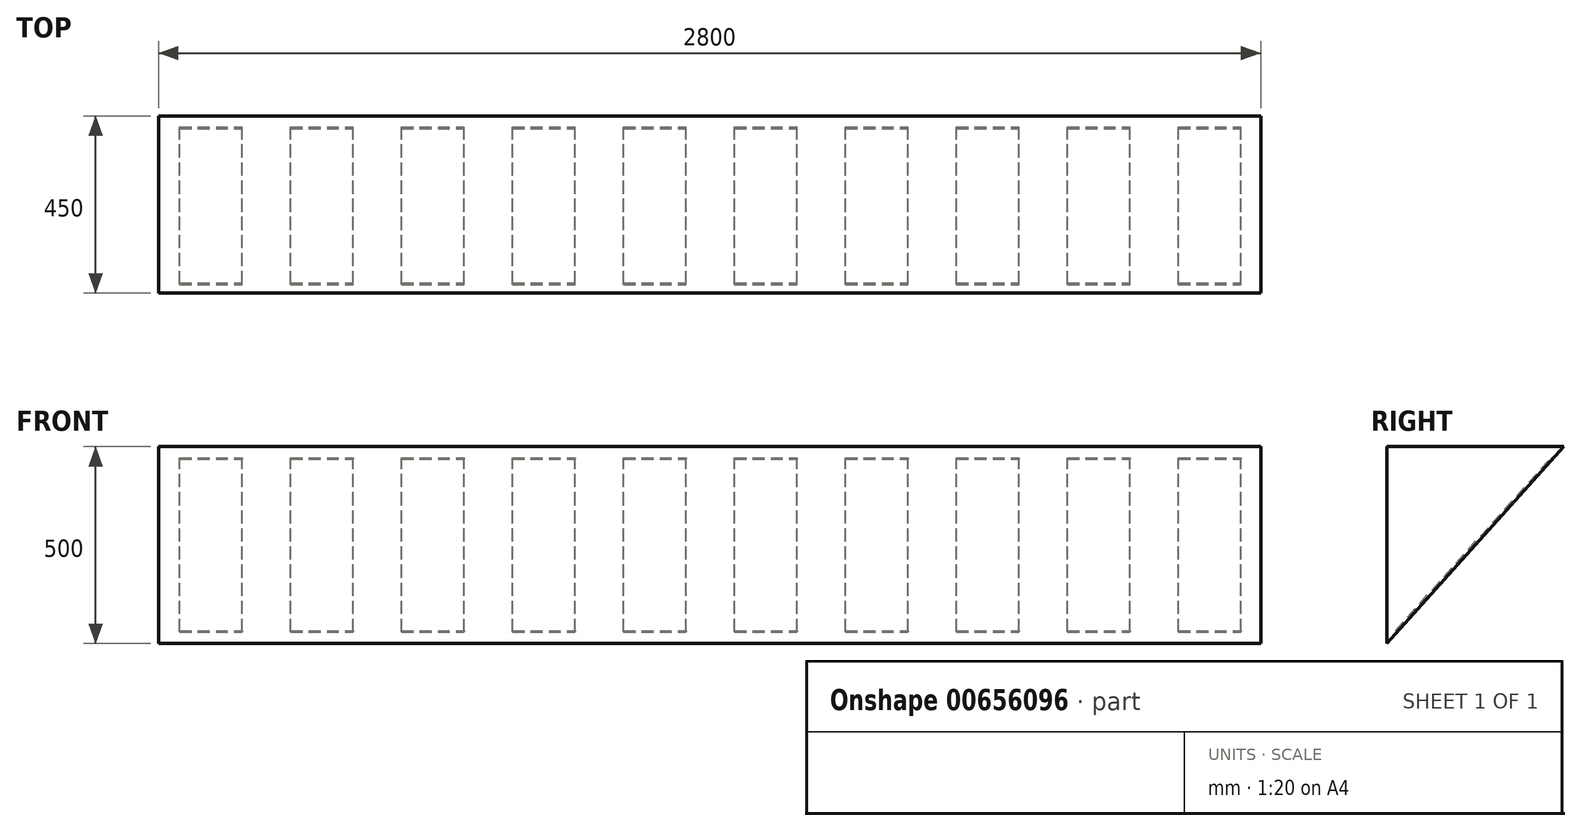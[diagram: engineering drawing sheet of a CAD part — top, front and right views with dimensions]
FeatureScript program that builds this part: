
annotation { "Feature Type Name" : "Feature", "Feature Type Description" : "" }
export const myFeature = defineFeature(function(context is Context, id is Id, definition is map)
    precondition{}
    {
        {
            var Q0;
            Q0=qCreatedBy(makeId("Right.planeOp"),FACE);
            var sketch = newSketch(context, id + "F0", { "sketchPlane" : qUnion([Q0])});
            skLineSegment(sketch, "E0", {"start": v(0, 0) * mm, "end": v(450, 0) * mm});
            skLineSegment(sketch, "E1", {"start": v(450, 0) * mm, "end": v(0, -500) * mm});
            skLineSegment(sketch, "E2", {"start": v(0, -500) * mm, "end": v(0, 0) * mm});
            skSolve(sketch);
        }
        {
            var Q0;
            Q0=makeQuery(id+"F0.imprint","IMPRINT",FACE,{"disambiguationData":[TD([[makeQuery(id+"F0.imprint","IMPRINT",EDGE,{"derivedFrom":sQuery(id+"F0.wireOp",EDGE,"E0")}),-1.0]])]});
            extrude(context, id + "F1", {"entities" : qUnion([Q0]), "depth" : 2800 * mm, "offsetDistance" : 25.4 * mm});
        }
        {
            var Q0;
            Q0=makeQuery(id+"F1.opExtrude","SWEPT_FACE",FACE,{"disambiguationData":[OSD([sQuery(id+"F0.wireOp",EDGE,"E1")])]});
            var sketch = newSketch(context, id + "F2", { "sketchPlane" : qUnion([Q0])});
            skLineSegment(sketch, "E3.bottom", {"start": v(-53.69, -332.56) * mm, "end": v(-212.32, -332.56) * mm});
            skLineSegment(sketch, "E3.top", {"start": v(-53.69, 258.3) * mm, "end": v(-212.32, 258.3) * mm});
            skLineSegment(sketch, "E3.left", {"start": v(-53.69, -332.56) * mm, "end": v(-53.69, 258.3) * mm});
            skLineSegment(sketch, "E3.right", {"start": v(-212.32, -332.56) * mm, "end": v(-212.32, 258.3) * mm});
            skLineSegment(sketch, "E4.1.0.0", {"start": v(-335.63, -332.56) * mm, "end": v(-494.26, -332.56) * mm});
            skLineSegment(sketch, "E4.1.0.1", {"start": v(-335.63, -332.56) * mm, "end": v(-335.63, 258.3) * mm});
            skLineSegment(sketch, "E4.1.0.2", {"start": v(-335.63, 258.3) * mm, "end": v(-494.26, 258.3) * mm});
            skLineSegment(sketch, "E4.1.0.3", {"start": v(-494.26, -332.56) * mm, "end": v(-494.26, 258.3) * mm});
            skLineSegment(sketch, "E4.2.0.0", {"start": v(-617.57, -332.56) * mm, "end": v(-776.2, -332.56) * mm});
            skLineSegment(sketch, "E4.2.0.1", {"start": v(-617.57, -332.56) * mm, "end": v(-617.57, 258.3) * mm});
            skLineSegment(sketch, "E4.2.0.2", {"start": v(-617.57, 258.3) * mm, "end": v(-776.2, 258.3) * mm});
            skLineSegment(sketch, "E4.2.0.3", {"start": v(-776.2, -332.56) * mm, "end": v(-776.2, 258.3) * mm});
            skLineSegment(sketch, "E4.3.0.0", {"start": v(-899.5, -332.56) * mm, "end": v(-1058.14, -332.56) * mm});
            skLineSegment(sketch, "E4.3.0.1", {"start": v(-899.5, -332.56) * mm, "end": v(-899.5, 258.3) * mm});
            skLineSegment(sketch, "E4.3.0.2", {"start": v(-899.5, 258.3) * mm, "end": v(-1058.14, 258.3) * mm});
            skLineSegment(sketch, "E4.3.0.3", {"start": v(-1058.14, -332.56) * mm, "end": v(-1058.14, 258.3) * mm});
            skLineSegment(sketch, "E4.4.0.0", {"start": v(-1181.45, -332.56) * mm, "end": v(-1340.08, -332.56) * mm});
            skLineSegment(sketch, "E4.4.0.1", {"start": v(-1181.45, -332.56) * mm, "end": v(-1181.45, 258.3) * mm});
            skLineSegment(sketch, "E4.4.0.2", {"start": v(-1181.45, 258.3) * mm, "end": v(-1340.08, 258.3) * mm});
            skLineSegment(sketch, "E4.4.0.3", {"start": v(-1340.08, -332.56) * mm, "end": v(-1340.08, 258.3) * mm});
            skLineSegment(sketch, "E4.5.0.0", {"start": v(-1463.39, -332.56) * mm, "end": v(-1622.02, -332.56) * mm});
            skLineSegment(sketch, "E4.5.0.1", {"start": v(-1463.39, -332.56) * mm, "end": v(-1463.39, 258.3) * mm});
            skLineSegment(sketch, "E4.5.0.2", {"start": v(-1463.39, 258.3) * mm, "end": v(-1622.02, 258.3) * mm});
            skLineSegment(sketch, "E4.5.0.3", {"start": v(-1622.02, -332.56) * mm, "end": v(-1622.02, 258.3) * mm});
            skLineSegment(sketch, "E4.6.0.0", {"start": v(-1745.33, -332.56) * mm, "end": v(-1903.96, -332.56) * mm});
            skLineSegment(sketch, "E4.6.0.1", {"start": v(-1745.33, -332.56) * mm, "end": v(-1745.33, 258.3) * mm});
            skLineSegment(sketch, "E4.6.0.2", {"start": v(-1745.33, 258.3) * mm, "end": v(-1903.96, 258.3) * mm});
            skLineSegment(sketch, "E4.6.0.3", {"start": v(-1903.96, -332.56) * mm, "end": v(-1903.96, 258.3) * mm});
            skLineSegment(sketch, "E4.7.0.0", {"start": v(-2027.27, -332.56) * mm, "end": v(-2185.9, -332.56) * mm});
            skLineSegment(sketch, "E4.7.0.1", {"start": v(-2027.27, -332.56) * mm, "end": v(-2027.27, 258.3) * mm});
            skLineSegment(sketch, "E4.7.0.2", {"start": v(-2027.27, 258.3) * mm, "end": v(-2185.9, 258.3) * mm});
            skLineSegment(sketch, "E4.7.0.3", {"start": v(-2185.9, -332.56) * mm, "end": v(-2185.9, 258.3) * mm});
            skLineSegment(sketch, "E4.8.0.0", {"start": v(-2309.2, -332.56) * mm, "end": v(-2467.84, -332.56) * mm});
            skLineSegment(sketch, "E4.8.0.1", {"start": v(-2309.2, -332.56) * mm, "end": v(-2309.2, 258.3) * mm});
            skLineSegment(sketch, "E4.8.0.2", {"start": v(-2309.2, 258.3) * mm, "end": v(-2467.84, 258.3) * mm});
            skLineSegment(sketch, "E4.8.0.3", {"start": v(-2467.84, -332.56) * mm, "end": v(-2467.84, 258.3) * mm});
            skLineSegment(sketch, "E4.9.0.0", {"start": v(-2591.15, -332.56) * mm, "end": v(-2749.78, -332.56) * mm});
            skLineSegment(sketch, "E4.9.0.1", {"start": v(-2591.15, -332.56) * mm, "end": v(-2591.15, 258.3) * mm});
            skLineSegment(sketch, "E4.9.0.2", {"start": v(-2591.15, 258.3) * mm, "end": v(-2749.78, 258.3) * mm});
            skLineSegment(sketch, "E4.9.0.3", {"start": v(-2749.78, -332.56) * mm, "end": v(-2749.78, 258.3) * mm});
            skLineSegment(sketch, "E4.direction1", {"start": v(-212.32, -332.56) * mm, "end": v(-494.26, -332.56) * mm, "construction": true});
            skSolve(sketch);
        }
        {
            var Q0;
            Q0=makeQuery(id+"F2.imprint","IMPRINT",FACE,{"disambiguationData":[TD([[makeQuery(id+"F2.imprint","IMPRINT",EDGE,{"derivedFrom":sQuery(id+"F2.wireOp",EDGE,"E4.9.0.0")}),-1.0]])]});
            var Q1;
            Q1=makeQuery(id+"F2.imprint","IMPRINT",FACE,{"disambiguationData":[TD([[makeQuery(id+"F2.imprint","IMPRINT",EDGE,{"derivedFrom":sQuery(id+"F2.wireOp",EDGE,"E4.8.0.0")}),-1.0]])]});
            var Q2;
            Q2=makeQuery(id+"F2.imprint","IMPRINT",FACE,{"disambiguationData":[TD([[makeQuery(id+"F2.imprint","IMPRINT",EDGE,{"derivedFrom":sQuery(id+"F2.wireOp",EDGE,"E4.7.0.0")}),-1.0]])]});
            var Q3;
            Q3=makeQuery(id+"F2.imprint","IMPRINT",FACE,{"disambiguationData":[TD([[makeQuery(id+"F2.imprint","IMPRINT",EDGE,{"derivedFrom":sQuery(id+"F2.wireOp",EDGE,"E4.6.0.0")}),-1.0]])]});
            var Q4;
            Q4=makeQuery(id+"F2.imprint","IMPRINT",FACE,{"disambiguationData":[TD([[makeQuery(id+"F2.imprint","IMPRINT",EDGE,{"derivedFrom":sQuery(id+"F2.wireOp",EDGE,"E4.5.0.0")}),-1.0]])]});
            var Q5;
            Q5=makeQuery(id+"F2.imprint","IMPRINT",FACE,{"disambiguationData":[TD([[makeQuery(id+"F2.imprint","IMPRINT",EDGE,{"derivedFrom":sQuery(id+"F2.wireOp",EDGE,"E4.4.0.0")}),-1.0]])]});
            var Q6;
            Q6=makeQuery(id+"F2.imprint","IMPRINT",FACE,{"disambiguationData":[TD([[makeQuery(id+"F2.imprint","IMPRINT",EDGE,{"derivedFrom":sQuery(id+"F2.wireOp",EDGE,"E4.3.0.0")}),-1.0]])]});
            var Q7;
            Q7=makeQuery(id+"F2.imprint","IMPRINT",FACE,{"disambiguationData":[TD([[makeQuery(id+"F2.imprint","IMPRINT",EDGE,{"derivedFrom":sQuery(id+"F2.wireOp",EDGE,"E4.2.0.0")}),-1.0]])]});
            var Q8;
            Q8=makeQuery(id+"F2.imprint","IMPRINT",FACE,{"disambiguationData":[TD([[makeQuery(id+"F2.imprint","IMPRINT",EDGE,{"derivedFrom":sQuery(id+"F2.wireOp",EDGE,"E4.1.0.0")}),-1.0]])]});
            var Q9;
            Q9=makeQuery(id+"F2.imprint","IMPRINT",FACE,{"disambiguationData":[TD([[makeQuery(id+"F2.imprint","IMPRINT",EDGE,{"derivedFrom":sQuery(id+"F2.wireOp",EDGE,"E3.bottom")}),-1.0]])]});
            extrude(context, id + "F3", {"entities" : qUnion([Q0, Q1, Q2, Q3, Q4, Q5, Q6, Q7, Q8, Q9]), "operationType" : NewBodyOperationType.REMOVE, "oppositeDirection" : true, "depth" : 5 * mm, "offsetDistance" : 25.4 * mm});
        }
    });
